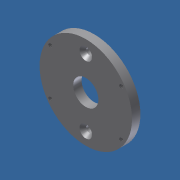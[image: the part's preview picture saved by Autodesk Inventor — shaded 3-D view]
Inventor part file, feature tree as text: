
AUTODESK INVENTOR PART (.ipt)
format: ipt  version: 2012 (Build 160160000, 160)  size: 97,792 bytes
history: native  units: in
note: dims shown in document units (in); Inventor stores cm internally (conversion verified against a paired STEP export)
features: hole x2, sketch x1, extrude x1
ambient origin geometry x8: Origin, YZ Plane, XZ Plane, XY Plane, X Axis, Y Axis, Z Axis, Center Point
bodies: Solid1 (feature_tree)
feature tree (4):
  sketch  "Sketch1"  dims[d0=2.75in d1=0.75in d2=1.0in d3=1.0in d4=1.055in d5=0.6875in d6=0.6875in d7=1.055in d8=0.25in d9=0.0in d10=0.104in d11=0.75in d12=0.375in d13=0.25in d14=0.5635in d15=1.0in d16=0.8108in d17=0.19in d18=0.339in d19=0.375in d20=0.25in d21=0.5635in d22=1.0in d23=0.8108in]
  extrude  "Extrusion1"  Depth=0.75in
  hole  "Hole1"  [1 undecoded]
  hole  "Hole2"  [1 undecoded]
note: 2 required parameter values undecoded (feature->parameter linkage not recoverable at this tier; creation-order binding heuristic only, values carry confidence <= 0.55)
